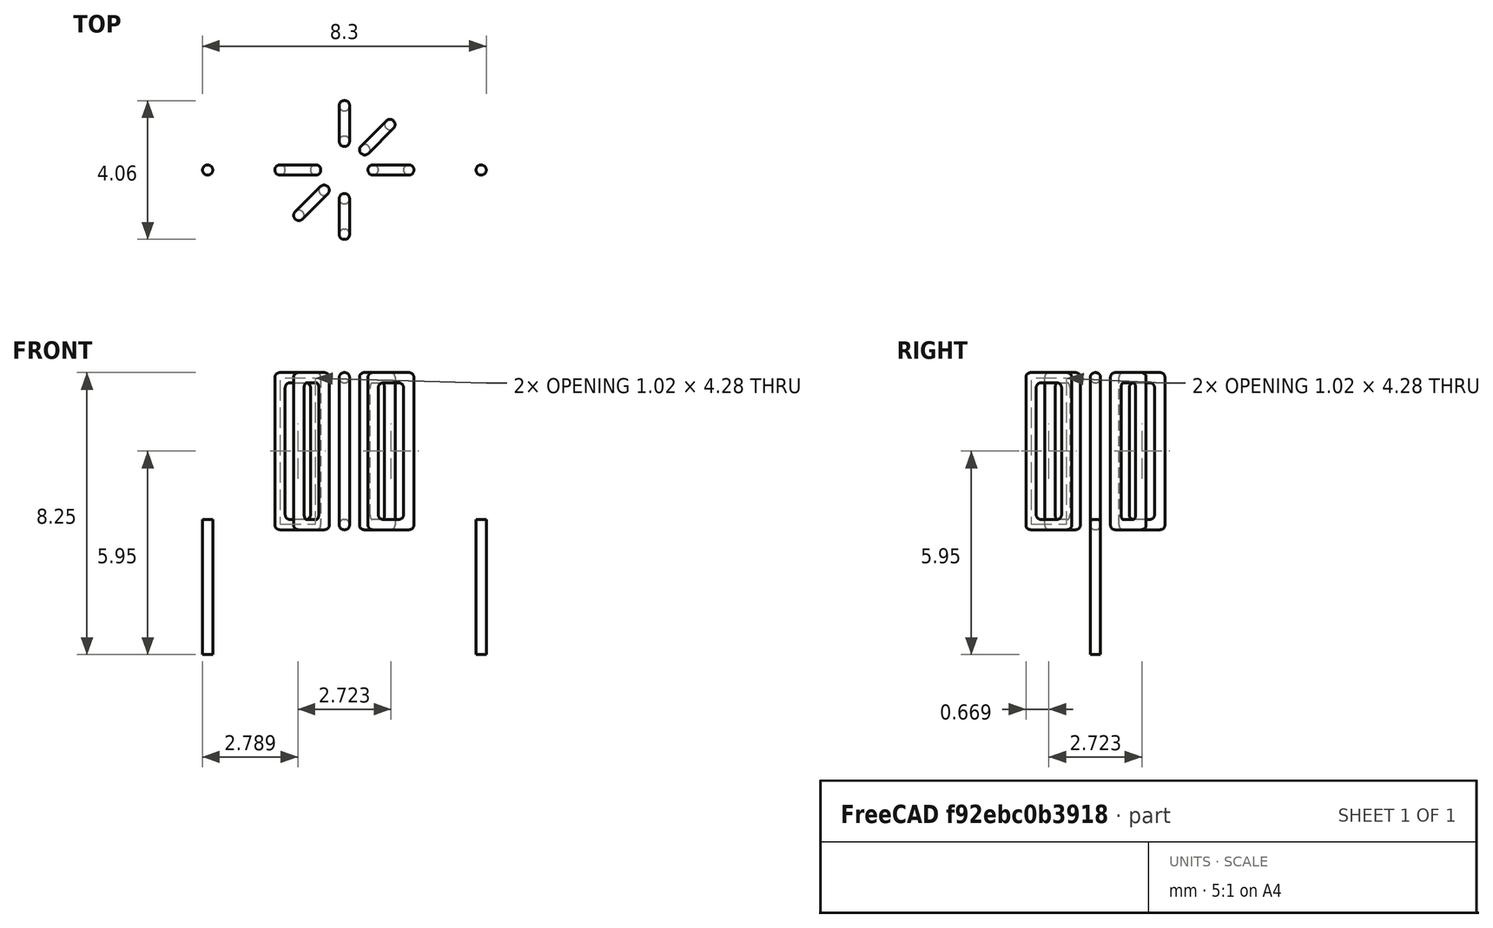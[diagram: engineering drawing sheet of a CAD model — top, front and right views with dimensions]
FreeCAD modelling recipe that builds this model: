
FCSTD DOCUMENT  (FreeCAD 0.16R6703 (Git))
Label: L_Toroid_Horizontal_D4.1mm_P8.00mm_Diameter4-5mm_Amidon-T16
License: All rights reserved
LicenseURL: http://en.wikipedia.org/wiki/All_rights_reserved
objects: Sketcher::SketchObject×6, PartDesign::Pad×6, PartDesign::Fillet×5, Spreadsheet::Sheet×1
note: 23 computed .brp shape members not serialized (recipe doc carries the construction recipe); baked Part::Feature solids carry a one-line shape summary decoded from their .brp

FEATURE [Spreadsheet::Sheet] Spreadsheet  label="dimensions"
  cells = A1=Wx; B1(Wx)=4.064; C1(WW)=1.9812; D1=4.064; A2=Wy; B2(Wy)=4.064; D2=4.064; A3=RM; B3(RMx)=8; C3(RMy)=0; A4=d_wire; B4(d_wire)=0.3; A5=H; B5(H)=4; A6=offsetx; B6(offsetx)=-1.968
FEATURE [Sketcher::SketchObject] Sketch
  Placement = pos=(0,0,0.8) rot=(0,0,1;0rad)
  expr: Placement.Base.z = 0.5 + Spreadsheet.d_wire
  expr: Constraints[0] = Spreadsheet.Wx / 2 - Spreadsheet.d_wire
  expr: Constraints[4] = Spreadsheet.WW / 2
  expr: Constraints[2] = Spreadsheet.RMy / 2
  expr: Constraints[1] = Spreadsheet.RMx / 2
  sketch-geometry (2):
    g0: Circle CenterX=4 CenterY=0 CenterZ=0 NormalX=0 NormalY=0 NormalZ=1 Radius=1.732
    g1: Circle CenterX=4 CenterY=0 CenterZ=0 NormalX=0 NormalY=0 NormalZ=1 Radius=0.9906
  constraints (5):
    c: Radius(g0) = 1.732
    c: DistanceX(g-1,g0) = 4
    c: DistanceY(g-1,g0) = 0
    c: Coincident(g1,g0)
    c: Radius(g1) = 0.9906
FEATURE [PartDesign::Pad] Pad
  Length = 4
  Length2 = 100
  Placement = pos=(0,0,0.8) rot=(0,0,1;0rad)
  Sketch = -> Sketch
  Type = 0
  expr: Length = Spreadsheet.H
FEATURE [Sketcher::SketchObject] Sketch001
  Placement = pos=(0,0,0.65) rot=(0,0,1;0rad)
  expr: Placement.Base.z = 0.5 + Spreadsheet.d_wire * 0.5
  expr: Constraints[4] = Spreadsheet.RMx
  expr: Constraints[2] = Spreadsheet.RMy
  expr: Constraints[1] = Spreadsheet.d_wire / 2
  sketch-geometry (2):
    g0: Circle CenterX=0 CenterY=0 CenterZ=0 NormalX=0 NormalY=0 NormalZ=1 Radius=0.15
    g1: Circle CenterX=8 CenterY=0 CenterZ=0 NormalX=0 NormalY=0 NormalZ=1 Radius=0.15
  constraints (5):
    c: Equal(g0,g1)
    c: Radius(g0) = 0.15
    c: DistanceY(g-1,g1) = 0
    c: Coincident(g0,g-1)
    c: DistanceX(g-1,g1) = 8
FEATURE [PartDesign::Pad] Pad001
  Length = 0.15
  Length2 = 3.8
  Placement = pos=(0,0,0.65) rot=(0,0,1;0rad)
  Reversed = true
  Sketch = -> Sketch001
  Type = 4
  expr: Length2 = 3.5 + Spreadsheet.d_wire
  expr: Length = Spreadsheet.d_wire / 2
FEATURE [PartDesign::Fillet] Fillet
  Base = -> Pad [Edge6,Edge3,Edge2]
  Placement = pos=(0,0,0.8) rot=(0,0,1;0rad)
  Radius = 0.5
FEATURE [Sketcher::SketchObject] Sketch003
  Placement = pos=(4,0,0) rot=(1,0,0;1.5708rad)
  expr: Placement.Base.x = Spreadsheet.RMx / 2
  expr: Constraints[49] = Spreadsheet.Wx - Spreadsheet.d_wire * 2
  expr: Constraints[44] = Spreadsheet.d_wire
  expr: Constraints[23] = Spreadsheet.H
  expr: Constraints[22] = Spreadsheet.Wx / 2 - Spreadsheet.d_wire
  expr: Placement.Base.y = Spreadsheet.RMy / 2
  expr: Constraints[21] = (Spreadsheet.Wx - Spreadsheet.WW) / 2 - Spreadsheet.d_wire
  expr: Constraints[19] = Spreadsheet.d_wire
  expr: Constraints[17] = Spreadsheet.d_wire
  expr: Constraints[18] = Spreadsheet.d_wire
  expr: Constraints[16] = Spreadsheet.d_wire
  sketch-geometry (16):
    g0: LineSegment StartX=-0.6906 StartY=0.5 StartZ=0 EndX=-2.032 EndY=0.5 EndZ=0
    g1: LineSegment StartX=-2.032 StartY=0.5 StartZ=0 EndX=-2.032 EndY=5.1 EndZ=0
    g2: LineSegment StartX=-2.032 StartY=5.1 StartZ=0 EndX=-0.6906 EndY=5.1 EndZ=0
    g3: LineSegment StartX=-0.6906 StartY=5.1 StartZ=0 EndX=-0.6906 EndY=0.5 EndZ=0
    g4: LineSegment StartX=-1.732 StartY=4.8 StartZ=0 EndX=-0.9906 EndY=4.8 EndZ=0
    g5: LineSegment StartX=-0.9906 StartY=4.8 StartZ=0 EndX=-0.9906 EndY=0.8 EndZ=0
    g6: LineSegment StartX=-0.9906 StartY=0.8 StartZ=0 EndX=-1.732 EndY=0.8 EndZ=0
    g7: LineSegment StartX=-1.732 StartY=0.8 StartZ=0 EndX=-1.732 EndY=4.8 EndZ=0
    g8: LineSegment StartX=0.6906 StartY=5.1 StartZ=0 EndX=2.032 EndY=5.1 EndZ=0
    g9: LineSegment StartX=2.032 StartY=5.1 StartZ=0 EndX=2.032 EndY=0.5 EndZ=0
    g10: LineSegment StartX=2.032 StartY=0.5 StartZ=0 EndX=0.6906 EndY=0.5 EndZ=0
    g11: LineSegment StartX=0.6906 StartY=0.5 StartZ=0 EndX=0.6906 EndY=5.1 EndZ=0
    g12: LineSegment StartX=0.9906 StartY=4.8 StartZ=0 EndX=1.732 EndY=4.8 EndZ=0
    g13: LineSegment StartX=1.732 StartY=4.8 StartZ=0 EndX=1.732 EndY=0.8 EndZ=0
    g14: LineSegment StartX=1.732 StartY=0.8 StartZ=0 EndX=0.9906 EndY=0.8 EndZ=0
    g15: LineSegment StartX=0.9906 StartY=0.8 StartZ=0 EndX=0.9906 EndY=4.8 EndZ=0
  constraints (50):
    c: Horizontal(g0)
    c: Coincident(g1,g0)
    c: Vertical(g1)
    c: Coincident(g2,g1)
    c: Horizontal(g2)
    c: Coincident(g3,g2)
    c: Coincident(g3,g0)
    c: Vertical(g3)
    c: Coincident(g4,g5)
    c: Coincident(g5,g6)
    c: Coincident(g6,g7)
    c: Coincident(g7,g4)
    c: Horizontal(g4)
    c: Horizontal(g6)
    c: Vertical(g5)
    c: Vertical(g7)
    c: DistanceX(g1,g4) = 0.3
    c: DistanceY(g4,g1) = 0.3
    c: DistanceX(g5,g0) = 0.3
    c: DistanceY(g0,g5) = 0.3
    c: DistanceY(g-1,g0) = 0.5
    c: DistanceX(g6,g6) = 0.7414
    c: DistanceX(g6,g-1) = 1.732
    c: DistanceY(g7,g7) = 4
    c: Coincident(g8,g9)
    c: Coincident(g9,g10)
    c: Coincident(g10,g11)
    c: Coincident(g11,g8)
    c: Horizontal(g8)
    c: Horizontal(g10)
    c: Vertical(g9)
    c: Vertical(g11)
    c: Coincident(g12,g13)
    c: Coincident(g13,g14)
    c: Coincident(g14,g15)
    c: Coincident(g15,g12)
    c: Horizontal(g12)
    c: Horizontal(g14)
    c: Vertical(g13)
    c: Vertical(g15)
    c: DistanceY(g8,g2) = 0
    c: DistanceY(g10,g0) = 0
    c: DistanceY(g14,g5) = 0
    c: DistanceY(g12,g4) = 0
    c: DistanceX(g8,g12) = 0.3
    c: Equal(g8,g2)
    c: Equal(g12,g4)
    c: Equal(g9,g1)
    c: Equal(g13,g7)
    c: DistanceX(g4,g12) = 3.464
FEATURE [PartDesign::Pad] Pad002
  Length = 0.3
  Length2 = 100
  Midplane = true
  Placement = pos=(4,0,0) rot=(1,0,0;1.5708rad)
  Sketch = -> Sketch003
  Type = 0
  expr: Length = Spreadsheet.d_wire
FEATURE [PartDesign::Fillet] Fillet001
  Base = -> Pad002 [Edge38,Edge41,Edge42,Edge43,Edge29,Edge32,Edge33,Edge34,Edge25,Edge35,Edge36,Edge13,Edge14,Edge15,Edge16,Edge17,Edge18,Edge19,Edge1,Edge2,Edge3,Edge4,Edge5,Edge6,Edge7,Edge37,Edge39,Edge40,Edge20,Edge23,Edge24,Edge21,Edge22,Edge8,Edge9,Edge10,Edge11,Edge12,Edge26,Edge27,+8 more]
  Placement = pos=(4,0,0) rot=(1,0,0;1.5708rad)
  Radius = 0.141
  expr: Radius = Spreadsheet.d_wire * 0.47
FEATURE [Sketcher::SketchObject] Sketch004
  Placement = pos=(4,0,0) rot=(0.862856,0.357407,0.357407;1.71777rad)
  expr: Placement.Base.x = Spreadsheet.RMx / 2
  expr: Constraints[49] = Spreadsheet.Wx - 2 * Spreadsheet.d_wire
  expr: Constraints[44] = Spreadsheet.d_wire
  expr: Constraints[23] = Spreadsheet.H
  expr: Constraints[22] = Spreadsheet.Wx / 2 - Spreadsheet.d_wire
  expr: Placement.Base.y = Spreadsheet.RMy / 2
  expr: Constraints[21] = (Spreadsheet.Wx - Spreadsheet.WW) / 2 - Spreadsheet.d_wire
  expr: Constraints[19] = Spreadsheet.d_wire
  expr: Constraints[17] = Spreadsheet.d_wire
  expr: Constraints[18] = Spreadsheet.d_wire
  expr: Constraints[16] = Spreadsheet.d_wire
  sketch-geometry (16):
    g0: LineSegment StartX=-0.6906 StartY=0.5 StartZ=0 EndX=-2.032 EndY=0.5 EndZ=0
    g1: LineSegment StartX=-2.032 StartY=0.5 StartZ=0 EndX=-2.032 EndY=5.1 EndZ=0
    g2: LineSegment StartX=-2.032 StartY=5.1 StartZ=0 EndX=-0.6906 EndY=5.1 EndZ=0
    g3: LineSegment StartX=-0.6906 StartY=5.1 StartZ=0 EndX=-0.6906 EndY=0.5 EndZ=0
    g4: LineSegment StartX=-1.732 StartY=4.8 StartZ=0 EndX=-0.9906 EndY=4.8 EndZ=0
    g5: LineSegment StartX=-0.9906 StartY=4.8 StartZ=0 EndX=-0.9906 EndY=0.8 EndZ=0
    g6: LineSegment StartX=-0.9906 StartY=0.8 StartZ=0 EndX=-1.732 EndY=0.8 EndZ=0
    g7: LineSegment StartX=-1.732 StartY=0.8 StartZ=0 EndX=-1.732 EndY=4.8 EndZ=0
    g8: LineSegment StartX=0.6906 StartY=5.1 StartZ=0 EndX=2.032 EndY=5.1 EndZ=0
    g9: LineSegment StartX=2.032 StartY=5.1 StartZ=0 EndX=2.032 EndY=0.5 EndZ=0
    g10: LineSegment StartX=2.032 StartY=0.5 StartZ=0 EndX=0.6906 EndY=0.5 EndZ=0
    g11: LineSegment StartX=0.6906 StartY=0.5 StartZ=0 EndX=0.6906 EndY=5.1 EndZ=0
    g12: LineSegment StartX=0.9906 StartY=4.8 StartZ=0 EndX=1.732 EndY=4.8 EndZ=0
    g13: LineSegment StartX=1.732 StartY=4.8 StartZ=0 EndX=1.732 EndY=0.8 EndZ=0
    g14: LineSegment StartX=1.732 StartY=0.8 StartZ=0 EndX=0.9906 EndY=0.8 EndZ=0
    g15: LineSegment StartX=0.9906 StartY=0.8 StartZ=0 EndX=0.9906 EndY=4.8 EndZ=0
  constraints (50):
    c: Horizontal(g0)
    c: Coincident(g1,g0)
    c: Vertical(g1)
    c: Coincident(g2,g1)
    c: Horizontal(g2)
    c: Coincident(g3,g2)
    c: Coincident(g3,g0)
    c: Vertical(g3)
    c: Coincident(g4,g5)
    c: Coincident(g5,g6)
    c: Coincident(g6,g7)
    c: Coincident(g7,g4)
    c: Horizontal(g4)
    c: Horizontal(g6)
    c: Vertical(g5)
    c: Vertical(g7)
    c: DistanceX(g1,g4) = 0.3
    c: DistanceY(g4,g1) = 0.3
    c: DistanceX(g5,g0) = 0.3
    c: DistanceY(g0,g5) = 0.3
    c: DistanceY(g-1,g0) = 0.5
    c: DistanceX(g6,g6) = 0.7414
    c: DistanceX(g6,g-1) = 1.732
    c: DistanceY(g7,g7) = 4
    c: Coincident(g8,g9)
    c: Coincident(g9,g10)
    c: Coincident(g10,g11)
    c: Coincident(g11,g8)
    c: Horizontal(g8)
    c: Horizontal(g10)
    c: Vertical(g9)
    c: Vertical(g11)
    c: Coincident(g12,g13)
    c: Coincident(g13,g14)
    c: Coincident(g14,g15)
    c: Coincident(g15,g12)
    c: Horizontal(g12)
    c: Horizontal(g14)
    c: Vertical(g13)
    c: Vertical(g15)
    c: DistanceY(g8,g2) = 0
    c: DistanceY(g10,g0) = 0
    c: DistanceY(g14,g5) = 0
    c: DistanceY(g12,g4) = 0
    c: DistanceX(g8,g12) = 0.3
    c: Equal(g8,g2)
    c: Equal(g12,g4)
    c: Equal(g9,g1)
    c: Equal(g13,g7)
    c: DistanceX(g4,g12) = 3.464
FEATURE [PartDesign::Pad] Pad003
  Length = 0.3
  Length2 = 100
  Midplane = true
  Placement = pos=(4,0,0) rot=(0.862856,0.357407,0.357407;1.71777rad)
  Sketch = -> Sketch004
  Type = 0
  expr: Length = Spreadsheet.d_wire
FEATURE [PartDesign::Fillet] Fillet002
  Base = -> Pad003 [Edge38,Edge41,Edge42,Edge43,Edge29,Edge32,Edge33,Edge34,Edge25,Edge35,Edge36,Edge13,Edge14,Edge15,Edge16,Edge17,Edge18,Edge19,Edge1,Edge2,Edge3,Edge4,Edge5,Edge6,Edge7,Edge37,Edge39,Edge40,Edge20,Edge23,Edge24,Edge21,Edge22,Edge8,Edge9,Edge10,Edge11,Edge12,Edge26,Edge27,+8 more]
  Placement = pos=(4,0,0) rot=(0.862856,0.357407,0.357407;1.71777rad)
  Radius = 0.141
  expr: Radius = Spreadsheet.d_wire * 0.47
FEATURE [Sketcher::SketchObject] Sketch005
  Placement = pos=(4,0,0) rot=(0.862856,-0.357407,-0.357407;1.71777rad)
  expr: Placement.Base.x = Spreadsheet.RMx / 2
  expr: Constraints[49] = Spreadsheet.Wx - 2 * Spreadsheet.d_wire
  expr: Constraints[44] = Spreadsheet.d_wire
  expr: Constraints[23] = Spreadsheet.H
  expr: Constraints[22] = Spreadsheet.Wx / 2 - Spreadsheet.d_wire
  expr: Placement.Base.y = Spreadsheet.RMy / 2
  expr: Constraints[21] = (Spreadsheet.Wx - Spreadsheet.WW) / 2 - Spreadsheet.d_wire
  expr: Constraints[19] = Spreadsheet.d_wire
  expr: Constraints[17] = Spreadsheet.d_wire
  expr: Constraints[18] = Spreadsheet.d_wire
  expr: Constraints[16] = Spreadsheet.d_wire
  sketch-geometry (16):
    g0: LineSegment StartX=-0.6906 StartY=0.5 StartZ=0 EndX=-2.032 EndY=0.5 EndZ=0
    g1: LineSegment StartX=-2.032 StartY=0.5 StartZ=0 EndX=-2.032 EndY=5.1 EndZ=0
    g2: LineSegment StartX=-2.032 StartY=5.1 StartZ=0 EndX=-0.6906 EndY=5.1 EndZ=0
    g3: LineSegment StartX=-0.6906 StartY=5.1 StartZ=0 EndX=-0.6906 EndY=0.5 EndZ=0
    g4: LineSegment StartX=-1.732 StartY=4.8 StartZ=0 EndX=-0.9906 EndY=4.8 EndZ=0
    g5: LineSegment StartX=-0.9906 StartY=4.8 StartZ=0 EndX=-0.9906 EndY=0.8 EndZ=0
    g6: LineSegment StartX=-0.9906 StartY=0.8 StartZ=0 EndX=-1.732 EndY=0.8 EndZ=0
    g7: LineSegment StartX=-1.732 StartY=0.8 StartZ=0 EndX=-1.732 EndY=4.8 EndZ=0
    g8: LineSegment StartX=0.6906 StartY=5.1 StartZ=0 EndX=2.032 EndY=5.1 EndZ=0
    g9: LineSegment StartX=2.032 StartY=5.1 StartZ=0 EndX=2.032 EndY=0.5 EndZ=0
    g10: LineSegment StartX=2.032 StartY=0.5 StartZ=0 EndX=0.6906 EndY=0.5 EndZ=0
    g11: LineSegment StartX=0.6906 StartY=0.5 StartZ=0 EndX=0.6906 EndY=5.1 EndZ=0
    g12: LineSegment StartX=0.9906 StartY=4.8 StartZ=0 EndX=1.732 EndY=4.8 EndZ=0
    g13: LineSegment StartX=1.732 StartY=4.8 StartZ=0 EndX=1.732 EndY=0.8 EndZ=0
    g14: LineSegment StartX=1.732 StartY=0.8 StartZ=0 EndX=0.9906 EndY=0.8 EndZ=0
    g15: LineSegment StartX=0.9906 StartY=0.8 StartZ=0 EndX=0.9906 EndY=4.8 EndZ=0
  constraints (50):
    c: Horizontal(g0)
    c: Coincident(g1,g0)
    c: Vertical(g1)
    c: Coincident(g2,g1)
    c: Horizontal(g2)
    c: Coincident(g3,g2)
    c: Coincident(g3,g0)
    c: Vertical(g3)
    c: Coincident(g4,g5)
    c: Coincident(g5,g6)
    c: Coincident(g6,g7)
    c: Coincident(g7,g4)
    c: Horizontal(g4)
    c: Horizontal(g6)
    c: Vertical(g5)
    c: Vertical(g7)
    c: DistanceX(g1,g4) = 0.3
    c: DistanceY(g4,g1) = 0.3
    c: DistanceX(g5,g0) = 0.3
    c: DistanceY(g0,g5) = 0.3
    c: DistanceY(g-1,g0) = 0.5
    c: DistanceX(g6,g6) = 0.7414
    c: DistanceX(g6,g-1) = 1.732
    c: DistanceY(g7,g7) = 4
    c: Coincident(g8,g9)
    c: Coincident(g9,g10)
    c: Coincident(g10,g11)
    c: Coincident(g11,g8)
    c: Horizontal(g8)
    c: Horizontal(g10)
    c: Vertical(g9)
    c: Vertical(g11)
    c: Coincident(g12,g13)
    c: Coincident(g13,g14)
    c: Coincident(g14,g15)
    c: Coincident(g15,g12)
    c: Horizontal(g12)
    c: Horizontal(g14)
    c: Vertical(g13)
    c: Vertical(g15)
    c: DistanceY(g8,g2) = 0
    c: DistanceY(g10,g0) = 0
    c: DistanceY(g14,g5) = 0
    c: DistanceY(g12,g4) = 0
    c: DistanceX(g8,g12) = 0.3
    c: Equal(g8,g2)
    c: Equal(g12,g4)
    c: Equal(g9,g1)
    c: Equal(g13,g7)
    c: DistanceX(g4,g12) = 3.464
FEATURE [PartDesign::Pad] Pad004
  Length = 0.3
  Length2 = 100
  Midplane = true
  Placement = pos=(4,0,0) rot=(0.862856,-0.357407,-0.357407;1.71777rad)
  Sketch = -> Sketch005
  Type = 0
  expr: Length = Spreadsheet.d_wire
FEATURE [PartDesign::Fillet] Fillet003
  Base = -> Pad004 [Edge38,Edge41,Edge42,Edge43,Edge29,Edge32,Edge33,Edge34,Edge25,Edge35,Edge36,Edge13,Edge14,Edge15,Edge16,Edge17,Edge18,Edge19,Edge1,Edge2,Edge3,Edge4,Edge5,Edge6,Edge7,Edge37,Edge39,Edge40,Edge20,Edge23,Edge24,Edge21,Edge22,Edge8,Edge9,Edge10,Edge11,Edge12,Edge26,Edge27,+8 more]
  Placement = pos=(4,0,0) rot=(0.862856,-0.357407,-0.357407;1.71777rad)
  Radius = 0.141
  expr: Radius = Spreadsheet.d_wire * 0.47
FEATURE [Sketcher::SketchObject] Sketch006
  Placement = pos=(4,0,0) rot=(0.57735,0.57735,0.57735;2.0944rad)
  expr: Placement.Base.x = Spreadsheet.RMx / 2
  expr: Constraints[49] = Spreadsheet.Wx - Spreadsheet.d_wire * 2
  expr: Constraints[44] = Spreadsheet.d_wire
  expr: Constraints[23] = Spreadsheet.H
  expr: Constraints[22] = Spreadsheet.Wx / 2 - Spreadsheet.d_wire
  expr: Placement.Base.y = Spreadsheet.RMy / 2
  expr: Constraints[21] = (Spreadsheet.Wx - Spreadsheet.WW) / 2 - Spreadsheet.d_wire
  expr: Constraints[19] = Spreadsheet.d_wire
  expr: Constraints[17] = Spreadsheet.d_wire
  expr: Constraints[18] = Spreadsheet.d_wire
  expr: Constraints[16] = Spreadsheet.d_wire
  sketch-geometry (16):
    g0: LineSegment StartX=-0.6906 StartY=0.5 StartZ=0 EndX=-2.032 EndY=0.5 EndZ=0
    g1: LineSegment StartX=-2.032 StartY=0.5 StartZ=0 EndX=-2.032 EndY=5.1 EndZ=0
    g2: LineSegment StartX=-2.032 StartY=5.1 StartZ=0 EndX=-0.6906 EndY=5.1 EndZ=0
    g3: LineSegment StartX=-0.6906 StartY=5.1 StartZ=0 EndX=-0.6906 EndY=0.5 EndZ=0
    g4: LineSegment StartX=-1.732 StartY=4.8 StartZ=0 EndX=-0.9906 EndY=4.8 EndZ=0
    g5: LineSegment StartX=-0.9906 StartY=4.8 StartZ=0 EndX=-0.9906 EndY=0.8 EndZ=0
    g6: LineSegment StartX=-0.9906 StartY=0.8 StartZ=0 EndX=-1.732 EndY=0.8 EndZ=0
    g7: LineSegment StartX=-1.732 StartY=0.8 StartZ=0 EndX=-1.732 EndY=4.8 EndZ=0
    g8: LineSegment StartX=0.6906 StartY=5.1 StartZ=0 EndX=2.032 EndY=5.1 EndZ=0
    g9: LineSegment StartX=2.032 StartY=5.1 StartZ=0 EndX=2.032 EndY=0.5 EndZ=0
    g10: LineSegment StartX=2.032 StartY=0.5 StartZ=0 EndX=0.6906 EndY=0.5 EndZ=0
    g11: LineSegment StartX=0.6906 StartY=0.5 StartZ=0 EndX=0.6906 EndY=5.1 EndZ=0
    g12: LineSegment StartX=0.9906 StartY=4.8 StartZ=0 EndX=1.732 EndY=4.8 EndZ=0
    g13: LineSegment StartX=1.732 StartY=4.8 StartZ=0 EndX=1.732 EndY=0.8 EndZ=0
    g14: LineSegment StartX=1.732 StartY=0.8 StartZ=0 EndX=0.9906 EndY=0.8 EndZ=0
    g15: LineSegment StartX=0.9906 StartY=0.8 StartZ=0 EndX=0.9906 EndY=4.8 EndZ=0
  constraints (50):
    c: Horizontal(g0)
    c: Coincident(g1,g0)
    c: Vertical(g1)
    c: Coincident(g2,g1)
    c: Horizontal(g2)
    c: Coincident(g3,g2)
    c: Coincident(g3,g0)
    c: Vertical(g3)
    c: Coincident(g4,g5)
    c: Coincident(g5,g6)
    c: Coincident(g6,g7)
    c: Coincident(g7,g4)
    c: Horizontal(g4)
    c: Horizontal(g6)
    c: Vertical(g5)
    c: Vertical(g7)
    c: DistanceX(g1,g4) = 0.3
    c: DistanceY(g4,g1) = 0.3
    c: DistanceX(g5,g0) = 0.3
    c: DistanceY(g0,g5) = 0.3
    c: DistanceY(g-1,g0) = 0.5
    c: DistanceX(g6,g6) = 0.7414
    c: DistanceX(g6,g-1) = 1.732
    c: DistanceY(g7,g7) = 4
    c: Coincident(g8,g9)
    c: Coincident(g9,g10)
    c: Coincident(g10,g11)
    c: Coincident(g11,g8)
    c: Horizontal(g8)
    c: Horizontal(g10)
    c: Vertical(g9)
    c: Vertical(g11)
    c: Coincident(g12,g13)
    c: Coincident(g13,g14)
    c: Coincident(g14,g15)
    c: Coincident(g15,g12)
    c: Horizontal(g12)
    c: Horizontal(g14)
    c: Vertical(g13)
    c: Vertical(g15)
    c: DistanceY(g8,g2) = 0
    c: DistanceY(g10,g0) = 0
    c: DistanceY(g14,g5) = 0
    c: DistanceY(g12,g4) = 0
    c: DistanceX(g8,g12) = 0.3
    c: Equal(g8,g2)
    c: Equal(g12,g4)
    c: Equal(g9,g1)
    c: Equal(g13,g7)
    c: DistanceX(g4,g12) = 3.464
FEATURE [PartDesign::Pad] Pad005
  Length = 0.3
  Length2 = 100
  Midplane = true
  Placement = pos=(4,0,0) rot=(0.57735,0.57735,0.57735;2.0944rad)
  Sketch = -> Sketch006
  Type = 0
  expr: Length = Spreadsheet.d_wire
FEATURE [PartDesign::Fillet] Fillet004
  Base = -> Pad005 [Edge38,Edge41,Edge42,Edge43,Edge29,Edge32,Edge33,Edge34,Edge25,Edge35,Edge36,Edge13,Edge14,Edge15,Edge16,Edge17,Edge18,Edge19,Edge1,Edge2,Edge3,Edge4,Edge5,Edge6,Edge7,Edge37,Edge39,Edge40,Edge20,Edge23,Edge24,Edge21,Edge22,Edge8,Edge9,Edge10,Edge11,Edge12,Edge26,Edge27,+8 more]
  Placement = pos=(4,0,0) rot=(0.57735,0.57735,0.57735;2.0944rad)
  Radius = 0.141
  expr: Radius = Spreadsheet.d_wire * 0.47
